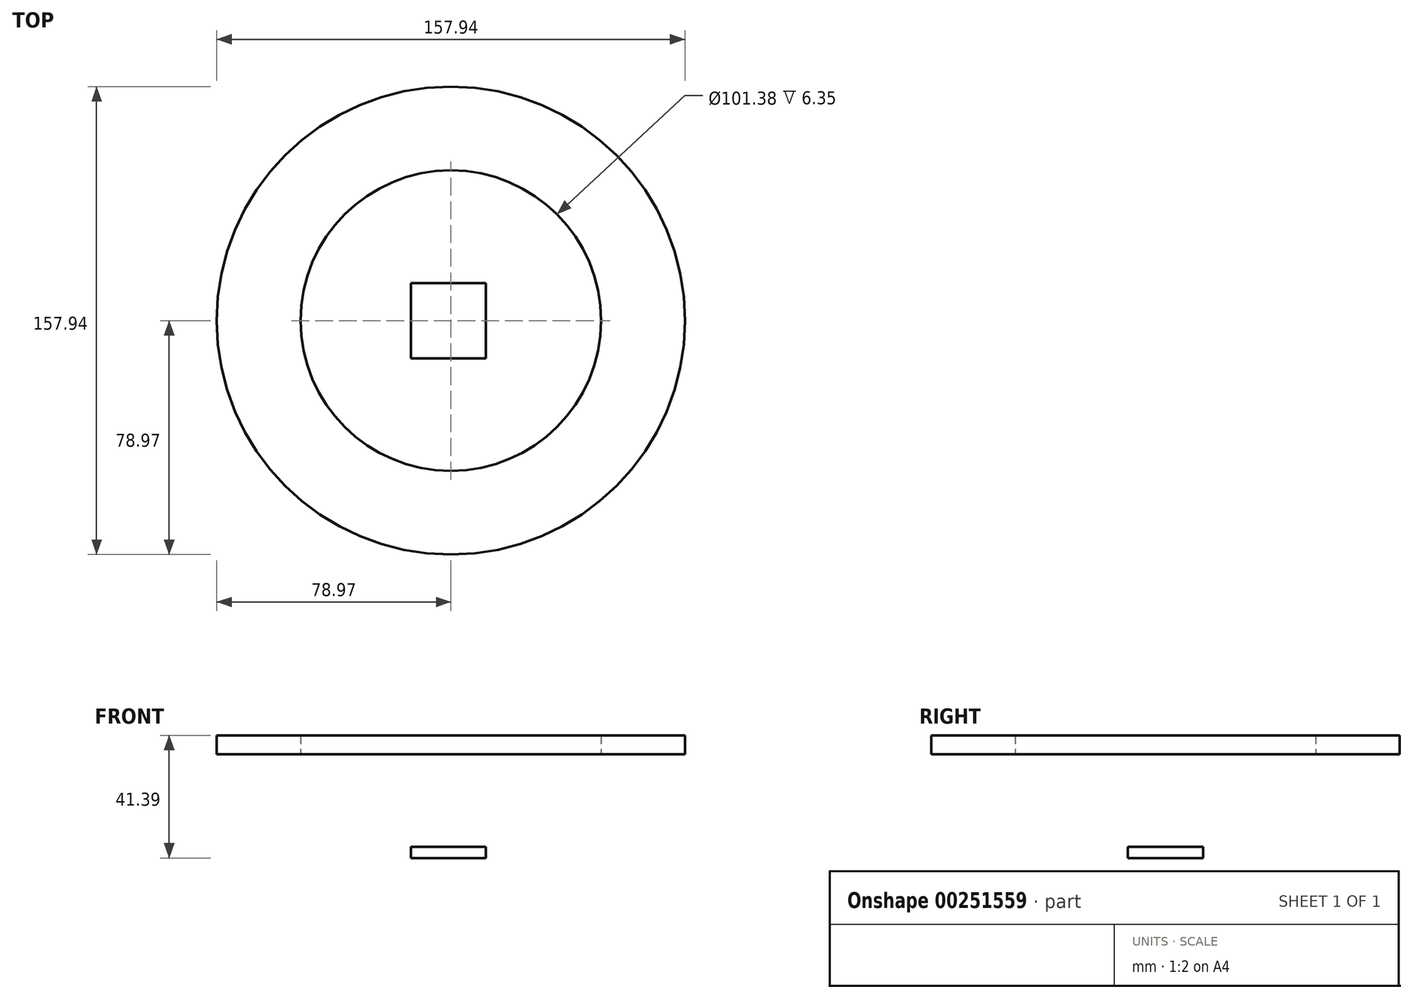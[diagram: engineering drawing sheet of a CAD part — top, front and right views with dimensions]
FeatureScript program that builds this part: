
annotation { "Feature Type Name" : "Feature", "Feature Type Description" : "" }
export const myFeature = defineFeature(function(context is Context, id is Id, definition is map)
    precondition{}
    {
        {
            var Q0;
            Q0=qCreatedBy(makeId("Top.planeOp"),FACE);
            var sketch = newSketch(context, id + "F0", { "sketchPlane" : qUnion([Q0])});
            skCircle(sketch, "E0", {"center": v(0, 0) * mm, "radius": 78.97 * mm});
            skCircle(sketch, "E1", {"center": v(0, 0) * mm, "radius": 50.7 * mm});
            skSolve(sketch);
        }
        {
            var Q0;
            Q0=qCreatedBy(makeId("Front.planeOp"),FACE);
            var sketch = newSketch(context, id + "F1", { "sketchPlane" : qUnion([Q0])});
            skLineSegment(sketch, "E2.bottom", {"start": v(-13.51, -31.24) * mm, "end": v(11.82, -31.24) * mm});
            skLineSegment(sketch, "E2.top", {"start": v(-13.51, -35.04) * mm, "end": v(11.82, -35.04) * mm});
            skLineSegment(sketch, "E2.left", {"start": v(-13.51, -31.24) * mm, "end": v(-13.51, -35.04) * mm});
            skLineSegment(sketch, "E2.right", {"start": v(11.82, -31.24) * mm, "end": v(11.82, -35.04) * mm});
            skSolve(sketch);
        }
        {
            var Q0;
            Q0=qSketchRegion(id+"F1",true);
            extrude(context, id + "F2", {"entities" : qUnion([Q0]), "endBound" : BoundingType.SYMMETRIC, "depth" : 25.4 * mm});
        }
        {
            var Q0;
            Q0=qCreatedBy(makeId("Right.planeOp"),FACE);
            var sketch = newSketch(context, id + "F3", { "sketchPlane" : qUnion([Q0])});
            skLineSegment(sketch, "E3", {"start": v(-10.2, -32.53) * mm, "end": v(-51.23, 0) * mm});
            skLineSegment(sketch, "E4", {"start": v(11.9, -33.7) * mm, "end": v(52.15, 0) * mm});
            skSolve(sketch);
        }
        {
            var Q0;
            Q0=qCreatedBy(makeId("Front.planeOp"),FACE);
            var sketch = newSketch(context, id + "F4", { "sketchPlane" : qUnion([Q0])});
            skLineSegment(sketch, "E5", {"start": v(-9.5, -34.11) * mm, "end": v(-52.26, 0) * mm});
            skLineSegment(sketch, "E6", {"start": v(10.53, -33.6) * mm, "end": v(51.4, 0) * mm});
            skSolve(sketch);
        }
        {
            var Q0;
            Q0=makeQuery(id+"F0.imprint","IMPRINT",FACE,{"disambiguationData":[TD([[makeQuery(id+"F0.imprint","IMPRINT",EDGE,{"derivedFrom":sQuery(id+"F0.wireOp",EDGE,"E0")}),1.0]])]});
            extrude(context, id + "F5", {"entities" : qUnion([Q0]), "depth" : 6.35 * mm});
        }
        {
            var Q0;
            Q0=sQuery(id+"F3.wireOp",EDGE,"E3");
            var Q1;
            Q1=sQuery(id+"F3.wireOp",EDGE,"E4");
            extrude(context, id + "F6", {"bodyType" : ToolBodyType.SURFACE, "surfaceEntities" : qUnion([Q0, Q1]), "endBound" : BoundingType.SYMMETRIC, "depth" : 6.35 * mm});
        }
        {
            var Q0;
            Q0=sQuery(id+"F4.wireOp",EDGE,"E6");
            var Q1;
            Q1=sQuery(id+"F4.wireOp",EDGE,"E5");
            extrude(context, id + "F7", {"bodyType" : ToolBodyType.SURFACE, "surfaceEntities" : qUnion([Q0, Q1]), "endBound" : BoundingType.SYMMETRIC, "depth" : 6.35 * mm});
        }
    });
